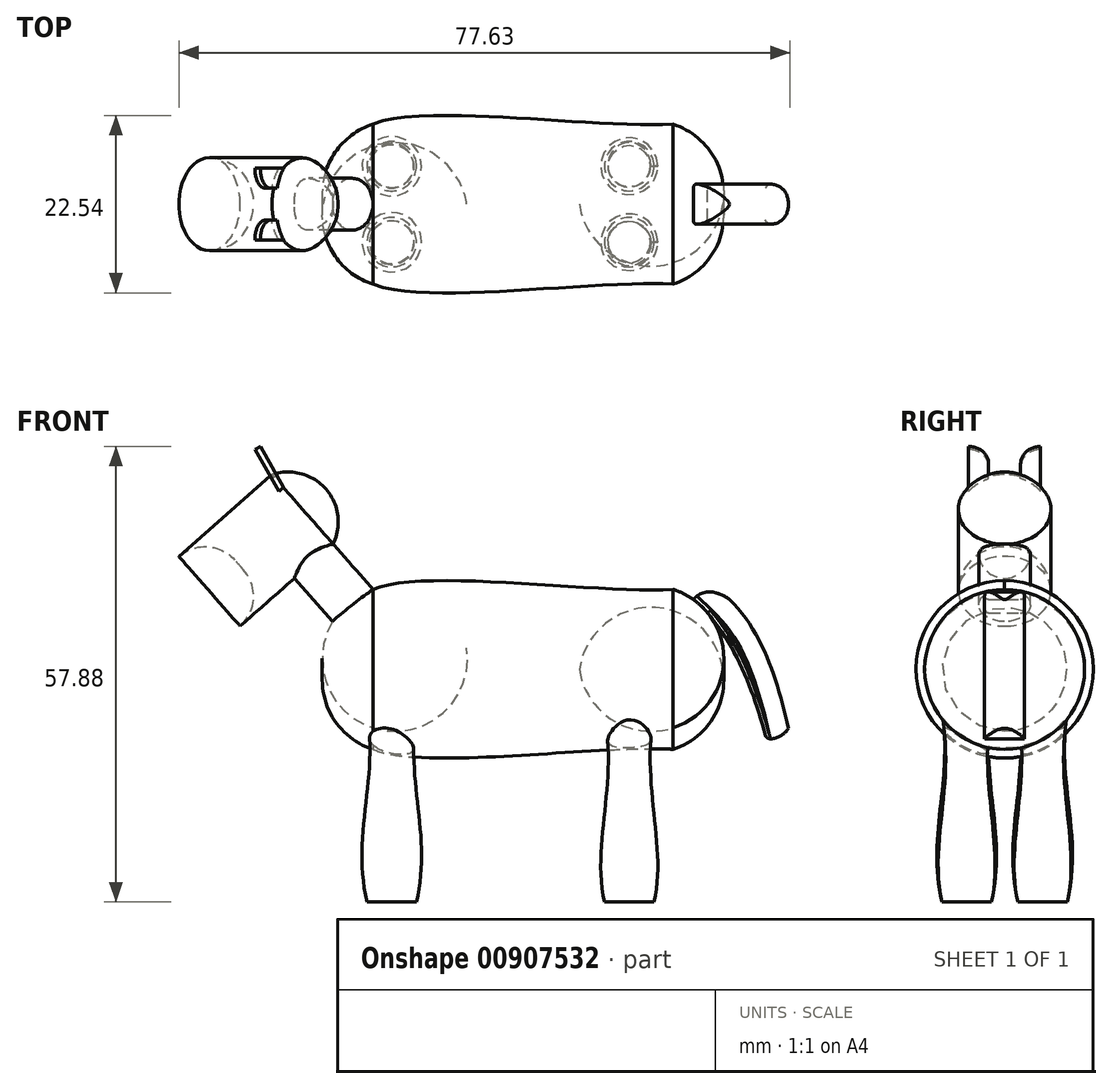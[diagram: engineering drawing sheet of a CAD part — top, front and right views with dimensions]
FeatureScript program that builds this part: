
annotation { "Feature Type Name" : "Feature", "Feature Type Description" : "" }
export const myFeature = defineFeature(function(context is Context, id is Id, definition is map)
    precondition{}
    {
        {
            var Q0;
            Q0=qCreatedBy(makeId("Front.planeOp"),FACE);
            var sketch = newSketch(context, id + "F0", { "sketchPlane" : qUnion([Q0])});
            skLineSegment(sketch, "E0", {"start": v(-28.72, 53.73) * mm, "end": v(-28.72, 43.57) * mm});
            skLineSegment(sketch, "E1", {"start": v(-28.72, 43.57) * mm, "end": v(9.38, 43.57) * mm});
            skLineSegment(sketch, "E2", {"start": v(9.38, 53.73) * mm, "end": v(9.38, 43.57) * mm});
            skFitSpline(sketch, "E3", {"points": [v(-28.72, 53.73) * mm, v(9.38, 53.73) * mm], "startDerivative": vector(18.74, 8.34) * mm, "endDerivative": vector(28.14, 1.83) * mm});
            skLineSegment(sketch, "E4", {"start": v(9.38, 43.57) * mm, "end": v(15.73, 43.57) * mm});
            skArc(sketch, "E5", {"start": v(15.73, 43.57) * mm, "mid": v(14.43, 49.82) * mm, "end": v(9.38, 53.73) * mm});
            skLineSegment(sketch, "E6", {"start": v(-28.72, 43.57) * mm, "end": v(-35.07, 43.57) * mm});
            skArc(sketch, "E7", {"start": v(-28.72, 53.73) * mm, "mid": v(-33.77, 49.82) * mm, "end": v(-35.07, 43.57) * mm});
            skLineSegment(sketch, "E8", {"start": v(-28.72, 53.73) * mm, "end": v(-37.67, 63.9) * mm});
            skLineSegment(sketch, "E9", {"start": v(-37.67, 63.9) * mm, "end": v(-40.14, 61.72) * mm});
            skLineSegment(sketch, "E10", {"start": v(-40.14, 61.72) * mm, "end": v(-31.7, 52.14) * mm});
            skLineSegment(sketch, "E11", {"start": v(-40.14, 61.72) * mm, "end": v(-44.03, 66.14) * mm});
            skLineSegment(sketch, "E12", {"start": v(-44.03, 66.14) * mm, "end": v(-41.56, 68.32) * mm});
            skLineSegment(sketch, "E13", {"start": v(-41.56, 68.32) * mm, "end": v(-37.67, 63.9) * mm});
            skLineSegment(sketch, "E14", {"start": v(-40.14, 61.72) * mm, "end": v(-53.22, 50.21) * mm});
            skLineSegment(sketch, "E15", {"start": v(-44.03, 66.14) * mm, "end": v(-53.39, 57.9) * mm});
            skArc(sketch, "E16", {"start": v(-53.39, 57.9) * mm, "mid": v(-55.1, 54.02) * mm, "end": v(-53.22, 50.21) * mm});
            skLineSegment(sketch, "E17", {"start": v(-37.67, 63.9) * mm, "end": v(-34.71, 66.5) * mm});
            skArc(sketch, "E18", {"start": v(-34.71, 66.5) * mm, "mid": v(-37.86, 68.43) * mm, "end": v(-41.56, 68.32) * mm});
            skFitSpline(sketch, "E19", {"points": [v(13.77, 50.74) * mm, v(21.2, 34.92) * mm], "startDerivative": vector(9.45, -11.09) * mm, "endDerivative": vector(6.14, -22.55) * mm});
            skFitSpline(sketch, "E20", {"points": [v(21.2, 34.92) * mm, v(24.05, 36.09) * mm], "startDerivative": vector(2.12, -1.53) * mm, "endDerivative": vector(1.6, 2.93) * mm});
            skFitSpline(sketch, "E21", {"points": [v(24.05, 36.09) * mm, v(16.55, 52.43) * mm], "startDerivative": vector(-4.2, 18.22) * mm, "endDerivative": vector(-12.64, 12.1) * mm});
            skFitSpline(sketch, "E22", {"points": [v(16.55, 52.43) * mm, v(11.97, 52.43) * mm], "startDerivative": vector(-3.9, 3.08) * mm, "endDerivative": vector(-3.55, -4.65) * mm});
            skSolve(sketch);
        }
        {
            var Q0;
            Q0=makeQuery(id+"F0.imprint","IMPRINT",FACE,{"disambiguationData":[TD([[makeQuery(id+"F0.imprint","IMPRINT",EDGE,{"derivedFrom":sQuery(id+"F0.wireOp",EDGE,"E0")}),1.0]])]});
            var Q1;
            {var subQ1=sQuery(id+"F0.wireOp",EDGE,"E2");var subQ3=sQuery(id+"F0.wireOp",EDGE,"eamPREXw-MF5n-ayYG-C2f2-R59Nyn2Oi9tY");var subQ4=makeQuery(id+"F0.imprint","INTERSECT",VERTEX,{"derivedFrom":[subQ1,subQ3]});Q1=makeQuery(id+"F0.imprint","IMPRINT",FACE,{"disambiguationData":[TD([[makeQuery(id+"F0.imprint","IMPRINT",EDGE,{"disambiguationData":[TD([[subQ4,1.0]])],"derivedFrom":subQ3}),1.0]])]});}
            var Q2;
            Q2=makeQuery(id+"F0.imprint","IMPRINT",FACE,{"disambiguationData":[TD([[makeQuery(id+"F0.imprint","IMPRINT",EDGE,{"derivedFrom":sQuery(id+"F0.wireOp",EDGE,"E2")}),1.0]])]});
            var Q3;
            Q3=makeQuery(id+"F0.imprint","IMPRINT",FACE,{"disambiguationData":[TD([[makeQuery(id+"F0.imprint","IMPRINT",EDGE,{"derivedFrom":sQuery(id+"F0.wireOp",EDGE,"E0")}),-1.0]])]});
            var Q4;
            Q4=sQuery(id+"F0.wireOp",EDGE,"E1");
            revolve(context, id + "F1", {"surfaceOperationType" : NewSurfaceOperationType.NEW, "entities" : qUnion([Q0, Q1, Q2, Q3]), "axis" : qUnion([Q4]), "revolveType" : RevolveType.FULL});
        }
        {
            var Q0;
            {var subQ0=sQuery(id+"F0.wireOp",EDGE,"E8");Q0=makeQuery(id+"F0.imprint","IMPRINT",FACE,{"disambiguationData":[TD([[makeQuery(id+"F0.imprint","IMPRINT",EDGE,{"derivedFrom":subQ0}),1.0]])]});}
            var Q1;
            Q1=sQuery(id+"F0.wireOp",EDGE,"E10");
            revolve(context, id + "F2", {"operationType" : NewBodyOperationType.ADD, "surfaceOperationType" : NewSurfaceOperationType.NEW, "entities" : qUnion([Q0]), "axis" : qUnion([Q1]), "revolveType" : RevolveType.FULL});
        }
        {
            var Q0;
            Q0=makeQuery(id+"F0.imprint","IMPRINT",FACE,{"disambiguationData":[TD([[makeQuery(id+"F0.imprint","IMPRINT",EDGE,{"derivedFrom":sQuery(id+"F0.wireOp",EDGE,"E11")}),1.0]])]});
            var Q1;
            Q1=makeQuery(id+"F0.imprint","IMPRINT",FACE,{"disambiguationData":[TD([[makeQuery(id+"F0.imprint","IMPRINT",EDGE,{"derivedFrom":sQuery(id+"F0.wireOp",EDGE,"E9")}),-1.0]])]});
            var Q2;
            Q2=makeQuery(id+"F0.imprint","IMPRINT",FACE,{"disambiguationData":[TD([[makeQuery(id+"F0.imprint","IMPRINT",EDGE,{"derivedFrom":sQuery(id+"F0.wireOp",EDGE,"E13")}),1.0]])]});
            var Q3;
            Q3=sQuery(id+"F0.wireOp",EDGE,"E9");
            revolve(context, id + "F3", {"operationType" : NewBodyOperationType.ADD, "surfaceOperationType" : NewSurfaceOperationType.NEW, "entities" : qUnion([Q0, Q1, Q2]), "axis" : qUnion([Q3]), "revolveType" : RevolveType.FULL});
        }
        {
            var Q0;
            Q0=qCreatedBy(makeId("Front.planeOp"),FACE);
            cPlane(context, id + "F4", {"entities" : qUnion([Q0]), "cplaneType" : CPlaneType.OFFSET, "offset" : 4.83 * mm, "width" : 152.4 * mm, "height" : 152.4 * mm});
        }
        {
            var Q0;
            Q0=qCreatedBy(id+"F4.planeOp",FACE);
            var sketch = newSketch(context, id + "F5", { "sketchPlane" : qUnion([Q0])});
            skLineSegment(sketch, "E23", {"start": v(-26.34, 37.74) * mm, "end": v(-26.34, 14) * mm});
            skLineSegment(sketch, "E24", {"start": v(-26.34, 14) * mm, "end": v(-29.48, 14) * mm});
            skLineSegment(sketch, "E25", {"start": v(-26.34, 37.74) * mm, "end": v(-29.48, 37.74) * mm});
            skFitSpline(sketch, "E26", {"points": [v(-29.48, 37.74) * mm, v(-29.48, 14) * mm], "startDerivative": vector(4.32, -24.56) * mm, "endDerivative": vector(6.02, -25.22) * mm});
            skLineSegment(sketch, "E27", {"start": v(-26.34, 37.74) * mm, "end": v(3.82, 37.74) * mm});
            skLineSegment(sketch, "E28", {"start": v(3.82, 37.74) * mm, "end": v(3.82, 14) * mm});
            skLineSegment(sketch, "E29", {"start": v(3.82, 37.74) * mm, "end": v(6.96, 37.74) * mm});
            skLineSegment(sketch, "E30", {"start": v(3.82, 14) * mm, "end": v(6.96, 14) * mm});
            skFitSpline(sketch, "E31", {"points": [v(6.96, 37.74) * mm, v(6.96, 14) * mm], "startDerivative": vector(-5.02, -26.26) * mm, "endDerivative": vector(-5, -21.68) * mm});
            skSolve(sketch);
        }
        {
            var Q0;
            Q0=makeQuery(id+"F5.imprint","IMPRINT",FACE,{"disambiguationData":[TD([[makeQuery(id+"F5.imprint","IMPRINT",EDGE,{"derivedFrom":sQuery(id+"F5.wireOp",EDGE,"E23")}),-1.0]])]});
            var Q1;
            Q1=sQuery(id+"F5.wireOp",EDGE,"E23");
            revolve(context, id + "F6", {"operationType" : NewBodyOperationType.ADD, "surfaceOperationType" : NewSurfaceOperationType.NEW, "entities" : qUnion([Q0]), "axis" : qUnion([Q1]), "revolveType" : RevolveType.FULL});
        }
        {
            var Q0;
            Q0=makeQuery(id+"F5.imprint","IMPRINT",FACE,{"disambiguationData":[TD([[makeQuery(id+"F5.imprint","IMPRINT",EDGE,{"derivedFrom":sQuery(id+"F5.wireOp",EDGE,"E28")}),1.0]])]});
            var Q1;
            Q1=sQuery(id+"F5.wireOp",EDGE,"E28");
            revolve(context, id + "F7", {"operationType" : NewBodyOperationType.ADD, "surfaceOperationType" : NewSurfaceOperationType.NEW, "entities" : qUnion([Q0]), "axis" : qUnion([Q1]), "revolveType" : RevolveType.FULL});
        }
        {
            var Q0;
            Q0=makeQuery(id+"F1.opRevolve","SWEPT_BODY",BODY,{"disambiguationData":[OSD([sQuery(id+"F0.wireOp",EDGE,"E1"),sQuery(id+"F0.wireOp",EDGE,"E3"),sQuery(id+"F0.wireOp",EDGE,"E4"),sQuery(id+"F0.wireOp",EDGE,"E5"),sQuery(id+"F0.wireOp",EDGE,"E6"),sQuery(id+"F0.wireOp",EDGE,"E7")])]});
            var Q1;
            Q1=qCreatedBy(makeId("Front.planeOp"),FACE);
            mirror(context, id + "F8", {"operationType" : NewBodyOperationType.ADD, "entities" : qUnion([Q0]), "mirrorPlane" : qUnion([Q1])});
        }
        {
            var Q0;
            Q0=qCreatedBy(makeId("Front.planeOp"),FACE);
            cPlane(context, id + "F9", {"entities" : qUnion([Q0]), "cplaneType" : CPlaneType.OFFSET, "offset" : 2.03 * mm, "oppositeDirection" : true, "width" : 152.4 * mm, "height" : 152.4 * mm});
        }
        {
            var Q0;
            Q0=qCreatedBy(id+"F9.planeOp",FACE);
            var sketch = newSketch(context, id + "F10", { "sketchPlane" : qUnion([Q0])});
            skLineSegment(sketch, "E32", {"start": v(-40.3, 65.54) * mm, "end": v(-43.72, 71.5) * mm});
            skLineSegment(sketch, "E33", {"start": v(-43.72, 71.5) * mm, "end": v(-43.04, 71.89) * mm});
            skLineSegment(sketch, "E34", {"start": v(-43.04, 71.89) * mm, "end": v(-39.7, 66.06) * mm});
            skLineSegment(sketch, "E35", {"start": v(-39.7, 66.06) * mm, "end": v(-40.3, 65.54) * mm});
            skSolve(sketch);
        }
        {
            var Q0;
            Q0=makeQuery(id+"F10.imprint","IMPRINT",FACE,{"disambiguationData":[TD([[makeQuery(id+"F10.imprint","IMPRINT",EDGE,{"derivedFrom":sQuery(id+"F10.wireOp",EDGE,"E32")}),-1.0]])]});
            extrude(context, id + "F11", {"entities" : qUnion([Q0]), "operationType" : NewBodyOperationType.ADD, "oppositeDirection" : true, "depth" : 2.54 * mm, "offsetDistance" : 25.4 * mm});
        }
        {
            var Q0;
            Q0=makeQuery(id+"F1.opRevolve","SWEPT_BODY",BODY,{"disambiguationData":[OSD([sQuery(id+"F0.wireOp",EDGE,"E1"),sQuery(id+"F0.wireOp",EDGE,"E3"),sQuery(id+"F0.wireOp",EDGE,"E4"),sQuery(id+"F0.wireOp",EDGE,"E5"),sQuery(id+"F0.wireOp",EDGE,"E6"),sQuery(id+"F0.wireOp",EDGE,"E7")])]});
            var Q1;
            Q1=qCreatedBy(makeId("Front.planeOp"),FACE);
            mirror(context, id + "F12", {"operationType" : NewBodyOperationType.ADD, "entities" : qUnion([Q0]), "mirrorPlane" : qUnion([Q1])});
        }
        {
            var Q0;
            {var subQ0=sQuery(id+"F0.wireOp",EDGE,"E19");Q0=makeQuery(id+"F0.imprint","IMPRINT",FACE,{"disambiguationData":[TD([[makeQuery(id+"F0.imprint","IMPRINT",EDGE,{"derivedFrom":subQ0}),1.0]])]});}
            extrude(context, id + "F13", {"entities" : qUnion([Q0]), "depth" : 2.54 * mm, "offsetDistance" : 25.4 * mm});
        }
        {
            var Q0;
            {var subQ0=sQuery(id+"F0.wireOp",EDGE,"E19");Q0=makeQuery(id+"F0.imprint","IMPRINT",FACE,{"disambiguationData":[TD([[makeQuery(id+"F0.imprint","IMPRINT",EDGE,{"derivedFrom":subQ0}),1.0]])]});}
            extrude(context, id + "F14", {"entities" : qUnion([Q0]), "operationType" : NewBodyOperationType.ADD, "oppositeDirection" : true, "depth" : 2.54 * mm, "offsetDistance" : 25.4 * mm});
        }
        {
            var Q0;
            Q0=makeQuery(id+"F14.opExtrude","CAP_EDGE",EDGE,{"disambiguationData":[OSD([sQuery(id+"F0.wireOp",EDGE,"E21")])],"isStart":false});
            var Q1;
            Q1=makeQuery(id+"F13.opExtrude","CAP_EDGE",EDGE,{"disambiguationData":[OSD([sQuery(id+"F0.wireOp",EDGE,"E21")])],"isStart":false});
            fillet(context, id + "F15", {"entities" : qUnion([Q0, Q1]), "radius" : 2.54 * mm, "tangentPropagation" : true, "allowEdgeOverflow" : false});
        }
        {
            var Q0;
            Q0=makeQuery(id+"F11.opExtrude","CAP_EDGE",EDGE,{"disambiguationData":[OSD([sQuery(id+"F10.wireOp",EDGE,"E33")])],"isStart":true});
            var Q1;
            Q1=makeQuery(id+"F12.opPattern","COPY",EDGE,{"derivedFrom":makeQuery(id+"F11.opExtrude","CAP_EDGE",EDGE,{"disambiguationData":[OSD([sQuery(id+"F10.wireOp",EDGE,"E33")])],"isStart":true}),"instanceName":"1"});
            fillet(context, id + "F16", {"entities" : qUnion([Q0, Q1]), "radius" : 2.54 * mm, "tangentPropagation" : true, "allowEdgeOverflow" : false});
        }
        {
            var Q0;
            Q0=makeQuery(id+"F13.opExtrude","CAP_EDGE",EDGE,{"disambiguationData":[OSD([sQuery(id+"F0.wireOp",EDGE,"E5")])],"isStart":false});
            var Q1;
            Q1=makeQuery(id+"F14.opExtrude","CAP_EDGE",EDGE,{"disambiguationData":[OSD([sQuery(id+"F0.wireOp",EDGE,"E5")])],"isStart":false});
            var Q2;
            Q2=makeQuery(id+"F14.opExtrude","CAP_EDGE",EDGE,{"disambiguationData":[OSD([sQuery(id+"F0.wireOp",EDGE,"E19")])],"isStart":false});
            var Q3;
            {var subQ0=sQuery(id+"F0.wireOp",EDGE,"E20");var subQ1=sQuery(id+"F0.wireOp",EDGE,"E19");Q3=makeQuery(id+"F14.boolean.opBoolean","MERGE",EDGE,{"derivedFrom":[makeQuery(id+"F13.opExtrude","SWEPT_EDGE",EDGE,{"disambiguationData":[OSD([subQ1,subQ0])]}),makeQuery(id+"F14.opExtrude","SWEPT_EDGE",EDGE,{"disambiguationData":[OSD([subQ1,subQ0])]})]});}
            var Q4;
            Q4=makeQuery(id+"F13.opExtrude","CAP_EDGE",EDGE,{"disambiguationData":[OSD([sQuery(id+"F0.wireOp",EDGE,"E19")])],"isStart":false});
            fillet(context, id + "F17", {"entities" : qUnion([Q0, Q1, Q2, Q3, Q4]), "radius" : 0.5 * mm, "tangentPropagation" : true, "allowEdgeOverflow" : false});
        }
    });
